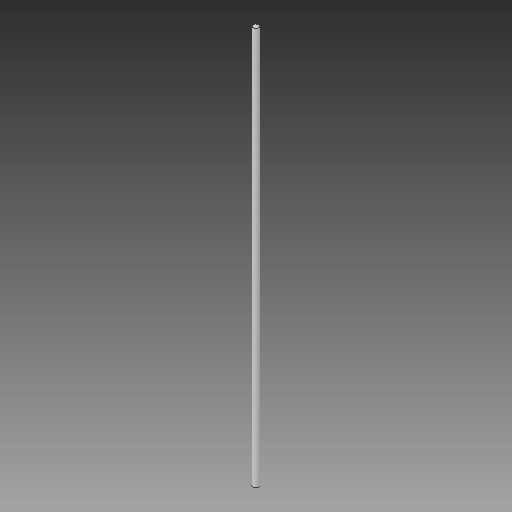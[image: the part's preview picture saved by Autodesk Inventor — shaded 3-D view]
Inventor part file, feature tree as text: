
AUTODESK INVENTOR PART (.ipt)
format: ipt  version: 2018 (Build 220112000, 112)  size: 72,704 bytes
history: native  units: mm
features: other x3, sketch x1
ambient origin geometry x8: Origin, YZ Plane, XZ Plane, XY Plane, X Axis, Y Axis, Z Axis, Center Point
bodies: Solid1 (feature_tree)
feature tree (4):
  other  "12mmSmoothRod_CPY.ipt"
  other  "Solid1::12mmSmoothRod_CPY.ipt"
  other  "TaggingFeature1"
  sketch  "Sketch1"  dims[d0=10.0mm]
